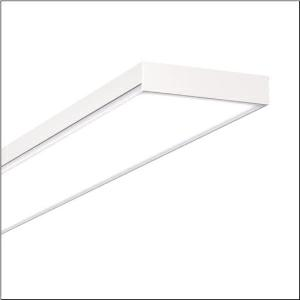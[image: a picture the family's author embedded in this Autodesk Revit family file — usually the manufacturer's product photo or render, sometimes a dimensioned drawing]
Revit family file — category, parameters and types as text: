
# Revit family: apollon_r__31_surface_51mp25wd2441wa_afb6
name_source: partatom
category: Lighting Fixtures
units: mm (PartAtom-declared; Revit-internal decimal feet)

## family parameters
Cut with Voids When Loaded = No
Host = Face
Light Source = No
Part Type = Normal
Room Calculation Point = No
Round Connector Dimension = Use Diameter
Shared = No

## types (1)
- Apollon® 31 Surface (1 x LED, 3800 lm, 28 W, 4000K)
    Apparent Load = 28 VA
    CIE Flux Codes = 61 87 97 97 100
    Color Rendering = 80
    Color Temperature = 4000K
    Default Elevation = 1800 mm
    Description = Apollon® 31 Surface, office luminaire, primary optical cover: micro prismatic cover, of PMMA, light emission: direct distribution, primary light characteristic: symmetric, installation type: surface-mounted, LED, rated luminous flux: 3.800lm, luminous efficacy: 134lm/W, light colour: 840, colour temperature: 4000K, control gear: ECG DALI, with terminal, 5-pole, mains connection: 220..240V, AC, 50/60Hz, rated input power: 28W, housing, of sheet steel, coil coated, traffic white (RAL 9016), length: 1.245mm, width: 200mm, height: 44mm, protection rating (complete): IP20, insulation class (complete): insulation class II (safety insulation), certification: CE, impact resistance: IK02, permissible operating ambient temperature: -20..+40°C, standard: EN 60598-2-22, packaging unit: 1 piece
    Height = 44 mm
    Lamp = 1 x LED
    Lamp Light Flux = 3800 lm
    Lamp Power = 28 W
    Lamp count = 1
    Length = 1245 mm
    Luminous efficacy = 136 lm/W
    Manufacturer = Siteco
    ModVariant = No
    Model = 51MP25WD2441WA
    Mounting Place = Ceiling
    Mounting Type = Surface mounted
    Number of Poles = 1
    OnlyDefault = Yes
    Power Factor = 1
    Product Name = Apollon® 31 Surface
    Product group = office luminaire | ceiling mounted
    ProductGroupID = 300
    Protection Class = Protection class II
    Protection Degree = IP 20
    RLX_Detail_Level = 1
    RLX_Emergency_Light_Flux = 0 lm
    RLX_Emergency_Type = 0
    RLX_Emergency_Type_DB = No
    RlxData = <blob elided: 20765 chars, md5=5f15d2af>
    Socket = socket
    Standby Power = 0 W
    System Light Flux = 3800 lm
    System Power = 28 W
    Type Comments = Product without accessories
    Type Image = l_1313658.jpg
    URL = http://relux.com
    VarID = ---
    Voltage = 0 V
    Weight = 0.00 kg
    Width = 200 mm  [stored 0.656168 ft]

note: [stored X ft] marks values corroborated as IEEE doubles in the binary element streams (Revit-internal decimal feet)

## geometry (parser evidence)
native form markers: Blend x4, Sweep x13
no freeform markers — native parametric forms only
